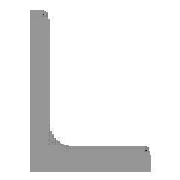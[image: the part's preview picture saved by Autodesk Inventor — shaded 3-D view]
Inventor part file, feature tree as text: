
AUTODESK INVENTOR PART (.ipt)
format: ipt  version: 2024.1 (Build 281209000, 209)  size: 120,832 bytes
history: native  units: mm (DEFAULTED — no unit token found)
features: other x4, sketch x1, plane x1
ambient origin geometry x8: Origin, YZ Plane, XZ Plane, XY Plane, X Axis, Y Axis, Z Axis, Center Point
bodies: Solid1 (feature_tree), Body (feature_tree)
feature tree (6):
  parser-record x1  (decoder bookkeeping rows leaked as tree rows — omitted from the tree; the rows remain in map.json)
  other  "Driven Length"
  other  "Start Plane"
  other  "End Plane"
  sketch  "Sketch3"  dims[d0=25.4mm d1=25.4mm d2=3.175mm d3=3.175mm d4=1300.0mm d5=0.0mm d10=0.0mm d11=0.0mm d12=-0.0mm d13=1300.0mm d14=3.302mm d15=1.524mm d16=90.0deg d17=1300.0mm]
  plane  "Work Plane3"
